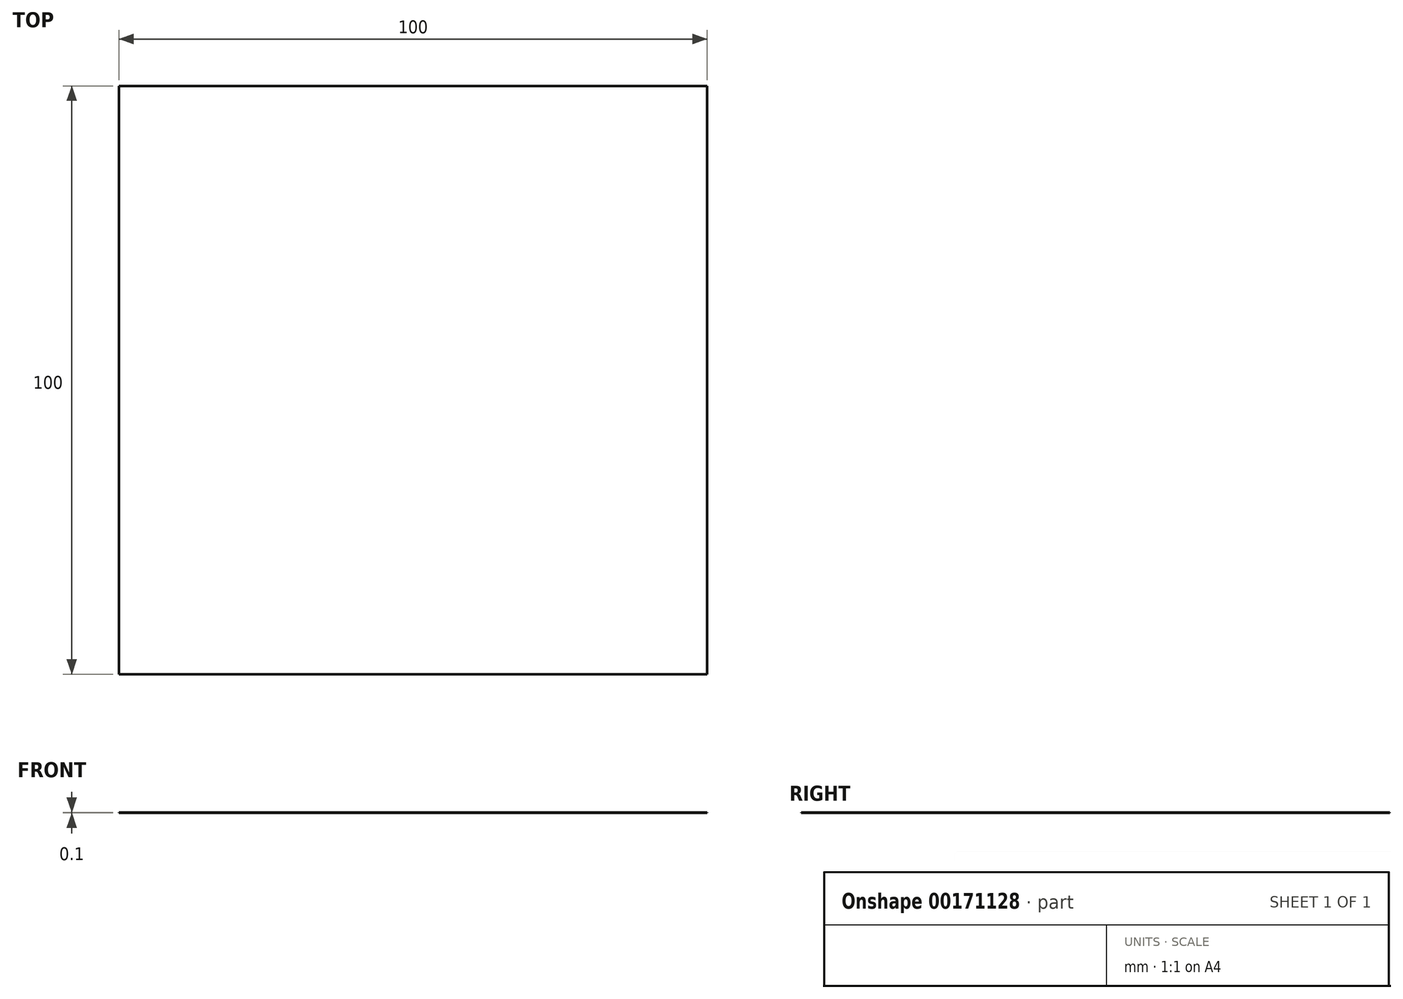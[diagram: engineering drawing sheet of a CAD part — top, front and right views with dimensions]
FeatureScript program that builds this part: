
annotation { "Feature Type Name" : "Feature", "Feature Type Description" : "" }
export const myFeature = defineFeature(function(context is Context, id is Id, definition is map)
    precondition{}
    {
        {
            var Q0;
            Q0=qCreatedBy(makeId("Top.planeOp"),FACE);
            var sketch = newSketch(context, id + "F0", { "sketchPlane" : qUnion([Q0])});
            skLineSegment(sketch, "E0.bottom", {"start": v(50, 50) * mm, "end": v(-50, 50) * mm});
            skLineSegment(sketch, "E0.top", {"start": v(50, -50) * mm, "end": v(-50, -50) * mm});
            skLineSegment(sketch, "E0.left", {"start": v(50, 50) * mm, "end": v(50, -50) * mm});
            skLineSegment(sketch, "E0.right", {"start": v(-50, 50) * mm, "end": v(-50, -50) * mm});
            skPoint(sketch, "E0.middle", {"position": v(0, 0) * mm});
            skSolve(sketch);
        }
        {
            var Q0;
            Q0 = qSketchRegion(id + "F0", true);
            extrude(context, id + "F1", {"entities" : qUnion([Q0]), "depth" : 0.1 * mm});
        }
    });
